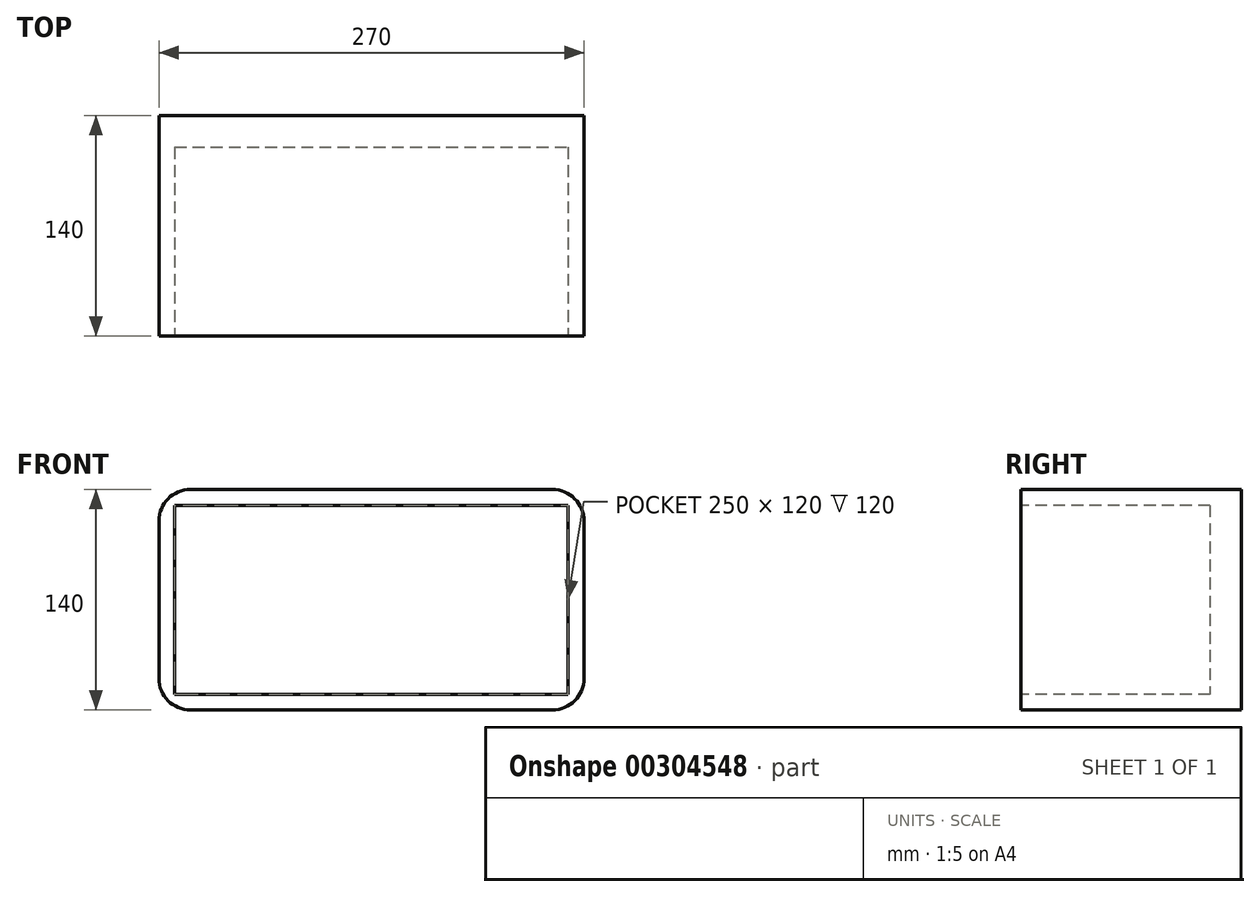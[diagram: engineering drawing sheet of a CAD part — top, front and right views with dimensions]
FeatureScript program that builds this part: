
annotation { "Feature Type Name" : "Feature", "Feature Type Description" : "" }
export const myFeature = defineFeature(function(context is Context, id is Id, definition is map)
    precondition{}
    {
        {
            var Q0;
            Q0=qCreatedBy(makeId("Front.planeOp"),FACE);
            var sketch = newSketch(context, id + "F0", { "sketchPlane" : qUnion([Q0])});
            skLineSegment(sketch, "E0.bottom", {"start": v(-135, 70) * mm, "end": v(135, 70) * mm});
            skLineSegment(sketch, "E0.top", {"start": v(-135, -70) * mm, "end": v(135, -70) * mm});
            skLineSegment(sketch, "E0.left", {"start": v(-135, 70) * mm, "end": v(-135, -70) * mm});
            skLineSegment(sketch, "E0.right", {"start": v(135, 70) * mm, "end": v(135, -70) * mm});
            skPoint(sketch, "E0.middle", {"position": v(0, 0) * mm});
            skSolve(sketch);
        }
        {
            var Q0;
            Q0 = qSketchRegion(id + "F0", true);
            extrude(context, id + "F1", {"entities" : qUnion([Q0]), "depth" : 140 * mm});
        }
        {
            var Q0;
            Q0=makeQuery(id+"F1.opExtrude","CAP_FACE",FACE,{"disambiguationData":[OSD([sQuery(id+"F0.wireOp",EDGE,"E0.bottom"),sQuery(id+"F0.wireOp",EDGE,"E0.top"),sQuery(id+"F0.wireOp",EDGE,"E0.left"),sQuery(id+"F0.wireOp",EDGE,"E0.right")])],"isStart":false});
            var sketch = newSketch(context, id + "F2", { "sketchPlane" : qUnion([Q0])});
            skLineSegment(sketch, "E1.bottom", {"start": v(-125, 60) * mm, "end": v(125, 60) * mm});
            skLineSegment(sketch, "E1.top", {"start": v(-125, -60) * mm, "end": v(125, -60) * mm});
            skLineSegment(sketch, "E1.left", {"start": v(-125, 60) * mm, "end": v(-125, -60) * mm});
            skLineSegment(sketch, "E1.right", {"start": v(125, 60) * mm, "end": v(125, -60) * mm});
            skPoint(sketch, "E1.middle", {"position": v(0, 0) * mm});
            skSolve(sketch);
        }
        {
            var Q0;
            Q0=makeQuery(id+"F2.imprint","IMPRINT",FACE,{"disambiguationData":[TD([[makeQuery(id+"F2.imprint","IMPRINT",EDGE,{"derivedFrom":sQuery(id+"F2.wireOp",EDGE,"E1.bottom")}),-1.0]])]});
            extrude(context, id + "F3", {"entities" : qUnion([Q0]), "operationType" : NewBodyOperationType.REMOVE, "oppositeDirection" : true, "depth" : 120 * mm});
        }
        {
            var Q0;
            Q0=makeQuery(id+"F1.opExtrude","SWEPT_EDGE",EDGE,{"disambiguationData":[OSD([sQuery(id+"F0.wireOp",EDGE,"E0.bottom"),sQuery(id+"F0.wireOp",EDGE,"E0.right")])]});
            var Q1;
            Q1=makeQuery(id+"F1.opExtrude","SWEPT_EDGE",EDGE,{"disambiguationData":[OSD([sQuery(id+"F0.wireOp",EDGE,"E0.bottom"),sQuery(id+"F0.wireOp",EDGE,"E0.left")])]});
            var Q2;
            Q2=makeQuery(id+"F1.opExtrude","SWEPT_EDGE",EDGE,{"disambiguationData":[OSD([sQuery(id+"F0.wireOp",EDGE,"E0.top"),sQuery(id+"F0.wireOp",EDGE,"E0.right")])]});
            var Q3;
            Q3=makeQuery(id+"F1.opExtrude","SWEPT_EDGE",EDGE,{"disambiguationData":[OSD([sQuery(id+"F0.wireOp",EDGE,"E0.top"),sQuery(id+"F0.wireOp",EDGE,"E0.left")])]});
            fillet(context, id + "F4", {"entities" : qUnion([Q0, Q1, Q2, Q3]), "radius" : 20 * mm, "tangentPropagation" : true, "allowEdgeOverflow" : false});
        }
    });
